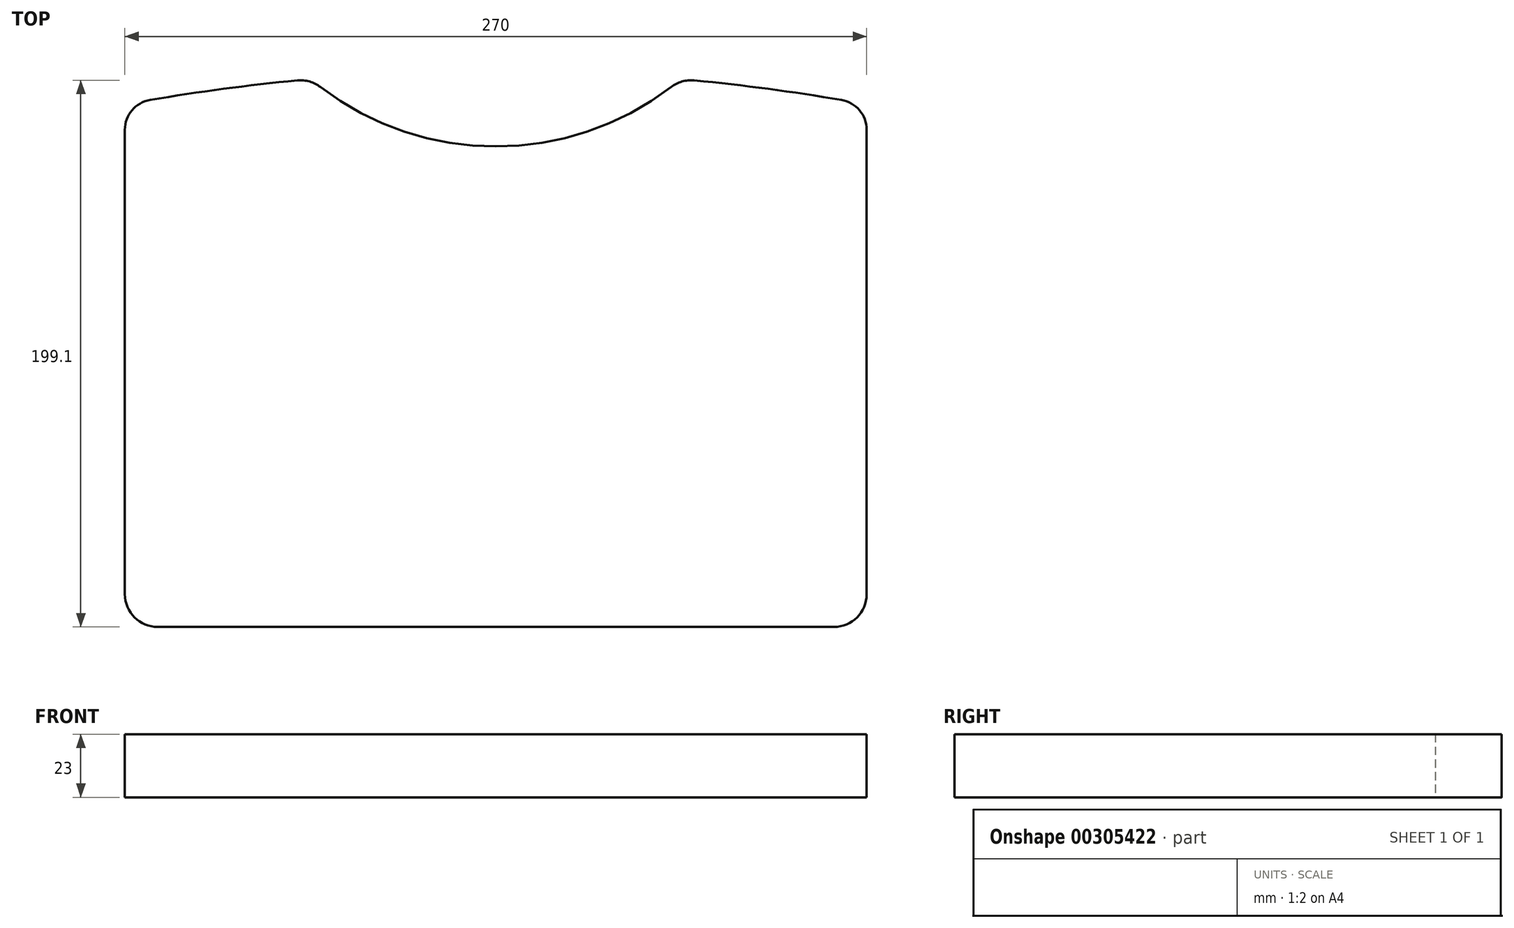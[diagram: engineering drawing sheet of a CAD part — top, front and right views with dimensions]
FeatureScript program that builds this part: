
annotation { "Feature Type Name" : "Feature", "Feature Type Description" : "" }
export const myFeature = defineFeature(function(context is Context, id is Id, definition is map)
    precondition{}
    {
        {
            var Q0;
            Q0=qCreatedBy(makeId("Top.planeOp"),FACE);
            var sketch = newSketch(context, id + "F0", { "sketchPlane" : qUnion([Q0])});
            skLineSegment(sketch, "E0.top", {"start": v(-123, -99.75) * mm, "end": v(123, -99.75) * mm});
            skLineSegment(sketch, "E0.left", {"start": v(-135, 81.33) * mm, "end": v(-135, -87.75) * mm});
            skLineSegment(sketch, "E0.right", {"start": v(135, 81.33) * mm, "end": v(135, -87.75) * mm});
            skLineSegment(sketch, "E1", {"start": v(-173.86, 75.25) * mm, "end": v(164.52, 75.25) * mm, "construction": true});
            skLineSegment(sketch, "E2", {"start": v(-50.1, 180.15) * mm, "end": v(39.06, 180.15) * mm, "construction": true});
            skLineSegment(sketch, "E3", {"start": v(39.06, 180.15) * mm, "end": v(39.06, 177.86) * mm});
            skLineSegment(sketch, "E4", {"start": v(0, 0) * mm, "end": v(0, 180.15) * mm, "construction": true});
            skArc(sketch, "E5", {"start": v(0, 75.25) * mm, "mid": v(-33.68, 80.8) * mm, "end": v(-63.8, 96.88) * mm});
            skArc(sketch, "E6", {"start": v(0, 75.25) * mm, "mid": v(33.68, 80.8) * mm, "end": v(63.8, 96.88) * mm});
            skPoint(sketch, "E7", {"position": v(0, -649.75) * mm});
            skArc(sketch, "E8", {"start": v(125.84, 92.18) * mm, "mid": v(99.1, 96.22) * mm, "end": v(72.24, 99.3) * mm});
            skArc(sketch, "E9.trimOffspring", {"start": v(-72.24, 99.3) * mm, "mid": v(-99.1, 96.22) * mm, "end": v(-125.84, 92.18) * mm});
            skPoint(sketch, "E10.visualSharp", {"position": v(67.38, 99.75) * mm});
            skArc(sketch, "E10.filletArc", {"start": v(72.24, 99.3) * mm, "mid": v(67.8, 98.89) * mm, "end": v(63.8, 96.88) * mm});
            skPoint(sketch, "E11.visualSharp", {"position": v(-67.38, 99.75) * mm});
            skArc(sketch, "E11.filletArc", {"start": v(-63.8, 96.88) * mm, "mid": v(-67.8, 98.89) * mm, "end": v(-72.24, 99.3) * mm});
            skPoint(sketch, "E12.visualSharp", {"position": v(-135, 90.56) * mm});
            skArc(sketch, "E12.filletArc", {"start": v(-125.84, 92.18) * mm, "mid": v(-132.4, 88.43) * mm, "end": v(-135, 81.33) * mm});
            skPoint(sketch, "E13.visualSharp", {"position": v(135, 90.56) * mm});
            skArc(sketch, "E13.filletArc", {"start": v(135, 81.33) * mm, "mid": v(132.4, 88.43) * mm, "end": v(125.84, 92.18) * mm});
            skPoint(sketch, "E14.visualSharp", {"position": v(135, -99.75) * mm});
            skArc(sketch, "E14.filletArc", {"start": v(123, -99.75) * mm, "mid": v(131.49, -96.24) * mm, "end": v(135, -87.75) * mm});
            skPoint(sketch, "E15.visualSharp", {"position": v(-135, -99.75) * mm});
            skArc(sketch, "E15.filletArc", {"start": v(-135, -87.75) * mm, "mid": v(-131.49, -96.24) * mm, "end": v(-123, -99.75) * mm});
            skSolve(sketch);
        }
        {
            var Q0;
            Q0=qSketchRegion(id+"F0",true);
            extrude(context, id + "F1", {"entities" : qUnion([Q0]), "depth" : 23 * mm});
        }
    });
